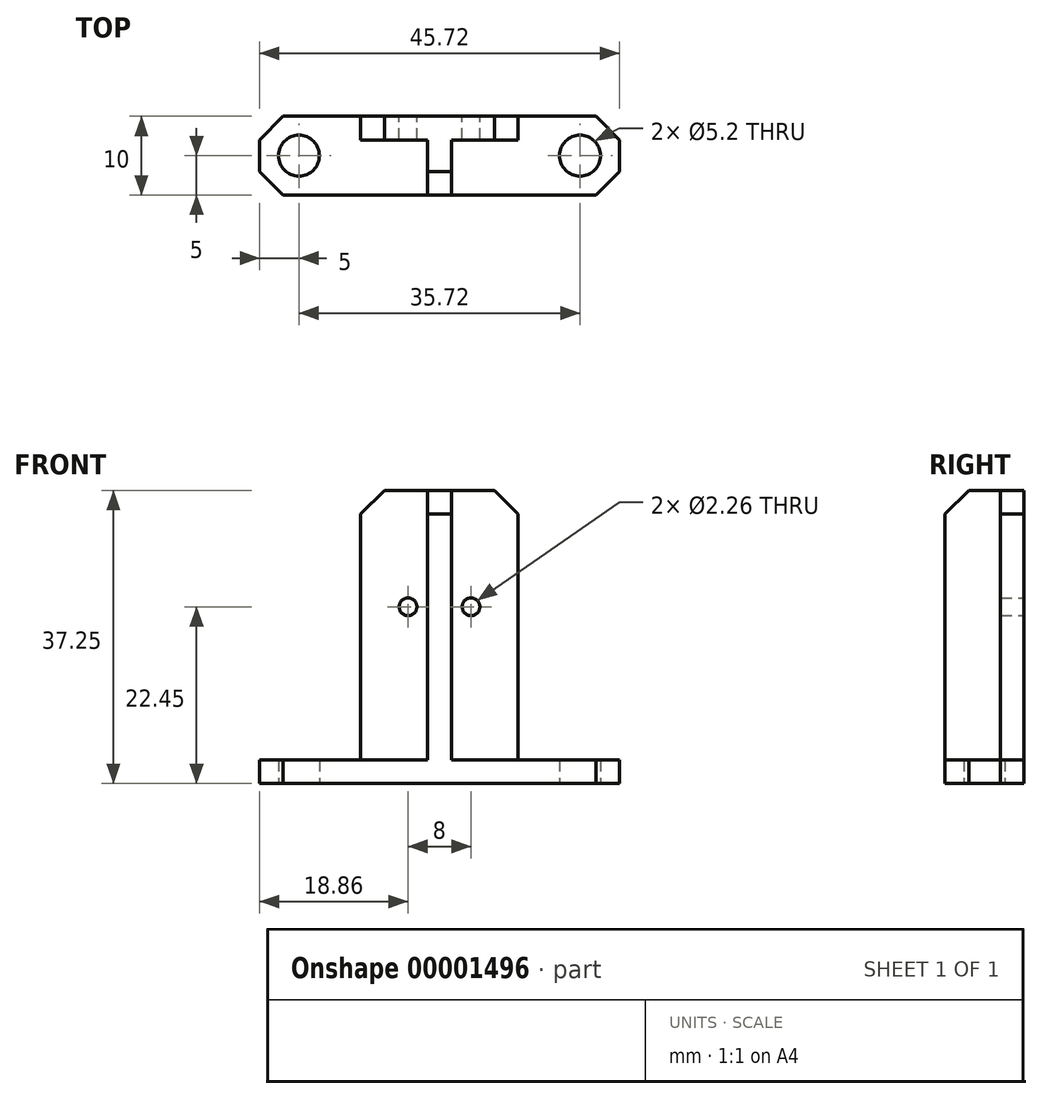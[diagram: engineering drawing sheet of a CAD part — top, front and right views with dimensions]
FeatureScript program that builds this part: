
annotation { "Feature Type Name" : "Feature", "Feature Type Description" : "" }
export const myFeature = defineFeature(function(context is Context, id is Id, definition is map)
    precondition{}
    {
        {
            var Q0;
            Q0=qCreatedBy(makeId("Top.planeOp"),FACE);
            var sketch = newSketch(context, id + "F0", { "sketchPlane" : qUnion([Q0])});
            skCircle(sketch, "E0", {"center": v(-17.86, 0) * mm, "radius": 2.6 * mm});
            skCircle(sketch, "E1", {"center": v(17.86, 0) * mm, "radius": 2.6 * mm});
            skLineSegment(sketch, "E2.bottom", {"start": v(-22.86, -5) * mm, "end": v(22.86, -5) * mm});
            skLineSegment(sketch, "E2.top", {"start": v(-22.86, 5) * mm, "end": v(22.86, 5) * mm});
            skLineSegment(sketch, "E2.left", {"start": v(-22.86, -5) * mm, "end": v(-22.86, 5) * mm});
            skLineSegment(sketch, "E2.right", {"start": v(22.86, -5) * mm, "end": v(22.86, 5) * mm});
            skPoint(sketch, "E3", {"position": v(0, 5) * mm});
            skPoint(sketch, "E4", {"position": v(22.86, 0) * mm});
            skSolve(sketch);
        }
        {
            var Q0;
            Q0=makeQuery(id+"F0.imprint","IMPRINT",FACE,{"disambiguationData":[TD([[makeQuery(id+"F0.imprint","IMPRINT",EDGE,{"derivedFrom":sQuery(id+"F0.wireOp",EDGE,"E0")}),-1.0]])]});
            extrude(context, id + "F1", {"entities" : qUnion([Q0]), "depth" : 3 * mm});
        }
        {
            var Q0;
            Q0=makeQuery(id+"F1.opExtrude","CAP_FACE",FACE,{"disambiguationData":[OSD([sQuery(id+"F0.wireOp",EDGE,"E0"),sQuery(id+"F0.wireOp",EDGE,"E1"),sQuery(id+"F0.wireOp",EDGE,"E2.bottom"),sQuery(id+"F0.wireOp",EDGE,"E2.top"),sQuery(id+"F0.wireOp",EDGE,"E2.left"),sQuery(id+"F0.wireOp",EDGE,"E2.right")])],"isStart":false});
            var sketch = newSketch(context, id + "F2", { "sketchPlane" : qUnion([Q0])});
            skLineSegment(sketch, "E5.bottom", {"start": v(-10, 5) * mm, "end": v(10, 5) * mm});
            skLineSegment(sketch, "E5.top", {"start": v(-10, 2) * mm, "end": v(10, 2) * mm});
            skLineSegment(sketch, "E5.left", {"start": v(-10, 5) * mm, "end": v(-10, 2) * mm});
            skLineSegment(sketch, "E5.right", {"start": v(10, 5) * mm, "end": v(10, 2) * mm});
            skPoint(sketch, "E6", {"position": v(0, 5) * mm});
            skSolve(sketch);
        }
        {
            var Q0;
            Q0=makeQuery(id+"F2.imprint","IMPRINT",FACE,{"disambiguationData":[TD([[makeQuery(id+"F2.imprint","IMPRINT",EDGE,{"derivedFrom":sQuery(id+"F2.wireOp",EDGE,"E5.bottom")}),-1.0]])]});
            extrude(context, id + "F3", {"entities" : qUnion([Q0]), "operationType" : NewBodyOperationType.ADD, "depth" : 34.25 * mm});
        }
        {
            var Q0;
            Q0=makeQuery(id+"F3.boolean.opBoolean","MERGE",FACE,{"derivedFrom":[makeQuery(id+"F1.opExtrude","SWEPT_FACE",FACE,{"disambiguationData":[OSD([sQuery(id+"F0.wireOp",EDGE,"E2.top")])]}),makeQuery(id+"F3.opExtrude","SWEPT_FACE",FACE,{"disambiguationData":[OSD([sQuery(id+"F2.wireOp",EDGE,"E5.bottom")])]})]});
            var sketch = newSketch(context, id + "F4", { "sketchPlane" : qUnion([Q0])});
            skCircle(sketch, "E7", {"center": v(-4, 22.45) * mm, "radius": 1.13 * mm});
            skCircle(sketch, "E8", {"center": v(4, 22.45) * mm, "radius": 1.13 * mm});
            skSolve(sketch);
        }
        {
            var Q0;
            {Q0=qUnion([makeQuery(id+"F4.imprint","IMPRINT",FACE,{"disambiguationData":[TD([[makeQuery(id+"F4.imprint","IMPRINT",EDGE,{"derivedFrom":sQuery(id+"F4.wireOp",EDGE,"E7")}),1.0]])]}),makeQuery(id+"F4.imprint","IMPRINT",FACE,{"disambiguationData":[TD([[makeQuery(id+"F4.imprint","IMPRINT",EDGE,{"derivedFrom":sQuery(id+"F4.wireOp",EDGE,"E8")}),1.0]])]})]);}
            extrude(context, id + "F5", {"entities" : qUnion([Q0]), "operationType" : NewBodyOperationType.REMOVE, "endBound" : BoundingType.THROUGH_ALL, "oppositeDirection" : true, "depth" : 25 * mm});
        }
        {
            var Q0;
            Q0=makeQuery(id+"F1.opExtrude","SWEPT_EDGE",EDGE,{"disambiguationData":[OSD([sQuery(id+"F0.wireOp",EDGE,"E2.bottom"),sQuery(id+"F0.wireOp",EDGE,"E2.right")])]});
            var Q1;
            Q1=makeQuery(id+"F1.opExtrude","SWEPT_EDGE",EDGE,{"disambiguationData":[OSD([sQuery(id+"F0.wireOp",EDGE,"E2.top"),sQuery(id+"F0.wireOp",EDGE,"E2.right")])]});
            var Q2;
            Q2=makeQuery(id+"F1.opExtrude","SWEPT_EDGE",EDGE,{"disambiguationData":[OSD([sQuery(id+"F0.wireOp",EDGE,"E2.bottom"),sQuery(id+"F0.wireOp",EDGE,"E2.left")])]});
            var Q3;
            Q3=makeQuery(id+"F1.opExtrude","SWEPT_EDGE",EDGE,{"disambiguationData":[OSD([sQuery(id+"F0.wireOp",EDGE,"E2.top"),sQuery(id+"F0.wireOp",EDGE,"E2.left")])]});
            var Q4;
            Q4=makeQuery(id+"F3.opExtrude","CAP_EDGE",EDGE,{"disambiguationData":[OSD([sQuery(id+"F2.wireOp",EDGE,"E5.left")])],"isStart":false});
            var Q5;
            Q5=makeQuery(id+"F3.opExtrude","CAP_EDGE",EDGE,{"disambiguationData":[OSD([sQuery(id+"F2.wireOp",EDGE,"E5.right")])],"isStart":false});
            chamfer(context, id + "F6", {"entities" : qUnion([Q0, Q1, Q2, Q3, Q4, Q5]), "width" : 3 * mm, "tangentPropagation" : true});
        }
        {
            var Q0;
            Q0=makeQuery(id+"F3.opExtrude","SWEPT_FACE",FACE,{"disambiguationData":[OSD([sQuery(id+"F2.wireOp",EDGE,"E5.top")])]});
            var sketch = newSketch(context, id + "F7", { "sketchPlane" : qUnion([Q0])});
            skLineSegment(sketch, "E9.bottom", {"start": v(1.5, 3) * mm, "end": v(-1.5, 3) * mm});
            skLineSegment(sketch, "E9.top", {"start": v(1.5, 37.25) * mm, "end": v(-1.5, 37.25) * mm});
            skLineSegment(sketch, "E9.left", {"start": v(1.5, 3) * mm, "end": v(1.5, 37.25) * mm});
            skLineSegment(sketch, "E9.right", {"start": v(-1.5, 3) * mm, "end": v(-1.5, 37.25) * mm});
            skPoint(sketch, "E10", {"position": v(0, 37.25) * mm});
            skSolve(sketch);
        }
        {
            var Q0;
            Q0=makeQuery(id+"F7.imprint","IMPRINT",FACE,{"disambiguationData":[TD([[makeQuery(id+"F7.imprint","IMPRINT",EDGE,{"derivedFrom":sQuery(id+"F7.wireOp",EDGE,"E9.bottom")}),1.0]])]});
            extrude(context, id + "F8", {"entities" : qUnion([Q0]), "operationType" : NewBodyOperationType.ADD, "depth" : 7 * mm});
        }
        {
            var Q0;
            Q0=makeQuery(id+"F8.opExtrude","CAP_EDGE",EDGE,{"disambiguationData":[OSD([sQuery(id+"F7.wireOp",EDGE,"E9.top")])],"isStart":false});
            chamfer(context, id + "F9", {"entities" : qUnion([Q0]), "width" : 3 * mm, "tangentPropagation" : true});
        }
    });
